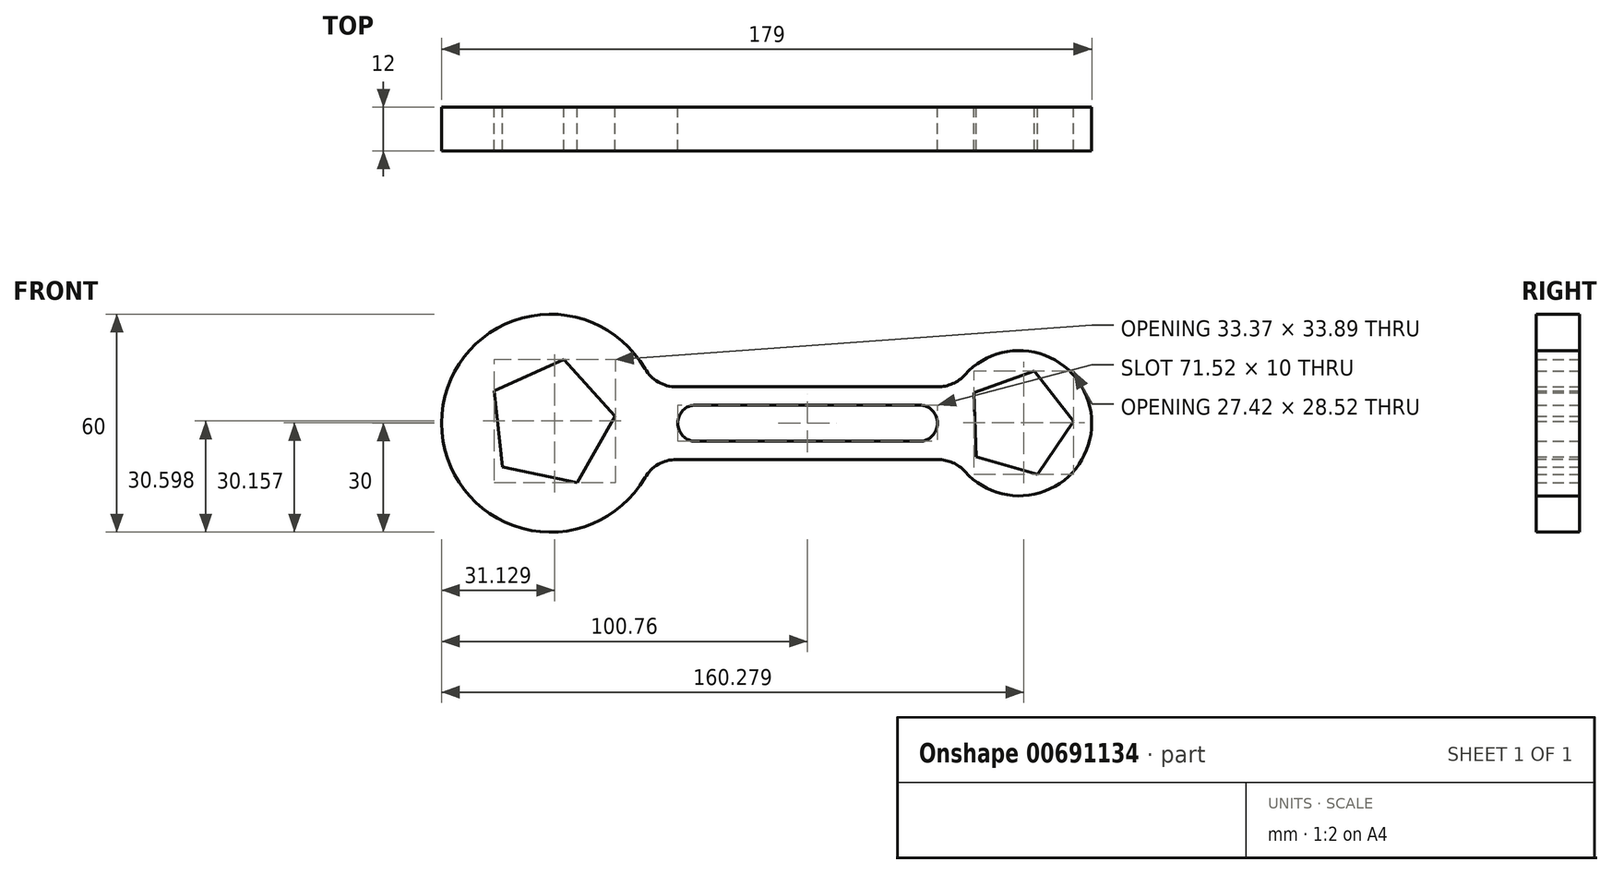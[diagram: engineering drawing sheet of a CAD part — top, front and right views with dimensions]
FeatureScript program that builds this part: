
annotation { "Feature Type Name" : "Feature", "Feature Type Description" : "" }
export const myFeature = defineFeature(function(context is Context, id is Id, definition is map)
    precondition{}
    {
        {
            var Q0;
            Q0=qCreatedBy(makeId("Front.planeOp"),FACE);
            var sketch = newSketch(context, id + "F0", { "sketchPlane" : qUnion([Q0])});
            skLineSegment(sketch, "E0.bottom", {"start": v(-42.92, 10) * mm, "end": v(40.48, 10) * mm});
            skLineSegment(sketch, "E0.top", {"start": v(-42.92, -10) * mm, "end": v(40.48, -10) * mm});
            skLineSegment(sketch, "E0.left", {"start": v(-42.92, 10) * mm, "end": v(-42.92, -10) * mm});
            skLineSegment(sketch, "E0.right", {"start": v(40.48, 10) * mm, "end": v(40.48, -10) * mm});
            skLineSegment(sketch, "E1.bottom", {"start": v(-31.2, 5) * mm, "end": v(30.32, 5) * mm});
            skLineSegment(sketch, "E1.top", {"start": v(-31.2, -5) * mm, "end": v(30.32, -5) * mm});
            skLineSegment(sketch, "E1.left", {"start": v(-31.2, 5) * mm, "end": v(-31.2, -5) * mm});
            skLineSegment(sketch, "E1.right", {"start": v(30.32, 5) * mm, "end": v(30.32, -5) * mm});
            skCircle(sketch, "E2", {"center": v(-31.2, 0) * mm, "radius": 5 * mm});
            skCircle(sketch, "E3", {"center": v(30.32, 0) * mm, "radius": 5 * mm});
            skCircle(sketch, "E4", {"center": v(-71.2, 0) * mm, "radius": 30 * mm});
            skCircle(sketch, "E5", {"center": v(57.8, 0) * mm, "radius": 20 * mm});
            skCircle(sketch, "E6.cCircle", {"center": v(-71.2, 0) * mm, "radius": 17.92 * mm, "construction": true});
            skLineSegment(sketch, "E6.0", {"start": v(-67.54, 17.54) * mm, "end": v(-53.39, 1.94) * mm});
            skLineSegment(sketch, "E6.1", {"start": v(-53.39, 1.94) * mm, "end": v(-63.86, -16.35) * mm});
            skLineSegment(sketch, "E6.2", {"start": v(-63.86, -16.35) * mm, "end": v(-84.48, -12.04) * mm});
            skLineSegment(sketch, "E6.3", {"start": v(-84.48, -12.04) * mm, "end": v(-86.75, 8.9) * mm});
            skLineSegment(sketch, "E6.4", {"start": v(-86.75, 8.9) * mm, "end": v(-67.54, 17.54) * mm});
            skCircle(sketch, "E7.cCircle", {"center": v(57.8, 0) * mm, "radius": 15 * mm, "construction": true});
            skLineSegment(sketch, "E7.0", {"start": v(61.95, 14.42) * mm, "end": v(72.8, 0.5) * mm});
            skLineSegment(sketch, "E7.1", {"start": v(72.8, 0.5) * mm, "end": v(62.91, -14.1) * mm});
            skLineSegment(sketch, "E7.2", {"start": v(62.91, -14.1) * mm, "end": v(45.97, -9.23) * mm});
            skLineSegment(sketch, "E7.3", {"start": v(45.97, -9.23) * mm, "end": v(45.37, 8.4) * mm});
            skLineSegment(sketch, "E7.4", {"start": v(45.37, 8.4) * mm, "end": v(61.95, 14.42) * mm});
            skSolve(sketch);
        }
        {
            var Q0;
            {var subQ1=sQuery(id+"F0.wireOp",EDGE,"E0.left");Q0=makeQuery(id+"F0.imprint","IMPRINT",FACE,{"disambiguationData":[TD([[makeQuery(id+"F0.imprint","IMPRINT",EDGE,{"derivedFrom":subQ1}),-1.0]])]});}
            var Q1;
            {var subQ3=sQuery(id+"F0.wireOp",EDGE,"E0.bottom");Q1=makeQuery(id+"F0.imprint","IMPRINT",FACE,{"disambiguationData":[TD([[makeQuery(id+"F0.imprint","IMPRINT",EDGE,{"derivedFrom":subQ3}),-1.0]])]});}
            var Q2;
            {var subQ0=sQuery(id+"F0.wireOp",EDGE,"E0.left");Q2=makeQuery(id+"F0.imprint","IMPRINT",FACE,{"disambiguationData":[TD([[makeQuery(id+"F0.imprint","IMPRINT",EDGE,{"derivedFrom":subQ0}),1.0]])]});}
            var Q3;
            {var subQ0=sQuery(id+"F0.wireOp",EDGE,"E0.right");Q3=makeQuery(id+"F0.imprint","IMPRINT",FACE,{"disambiguationData":[TD([[makeQuery(id+"F0.imprint","IMPRINT",EDGE,{"derivedFrom":subQ0}),-1.0]])]});}
            var Q4;
            {var subQ1=sQuery(id+"F0.wireOp",EDGE,"E0.right");Q4=makeQuery(id+"F0.imprint","IMPRINT",FACE,{"disambiguationData":[TD([[makeQuery(id+"F0.imprint","IMPRINT",EDGE,{"derivedFrom":subQ1}),1.0]])]});}
            extrude(context, id + "F1", {"entities" : qUnion([Q0, Q1, Q2, Q3, Q4]), "depth" : 12 * mm, "offsetDistance" : 25 * mm});
        }
        {
            var Q0;
            Q0=makeQuery(id+"F1.opExtrude","SWEPT_EDGE",EDGE,{"disambiguationData":[OSD([sQuery(id+"F0.wireOp",EDGE,"E0.top"),sQuery(id+"F0.wireOp",EDGE,"E0.left"),sQuery(id+"F0.wireOp",EDGE,"E4")])]});
            var Q1;
            Q1=makeQuery(id+"F1.opExtrude","SWEPT_EDGE",EDGE,{"disambiguationData":[OSD([sQuery(id+"F0.wireOp",EDGE,"E0.top"),sQuery(id+"F0.wireOp",EDGE,"E0.right"),sQuery(id+"F0.wireOp",EDGE,"E5")])]});
            var Q2;
            Q2=makeQuery(id+"F1.opExtrude","SWEPT_EDGE",EDGE,{"disambiguationData":[OSD([sQuery(id+"F0.wireOp",EDGE,"E0.bottom"),sQuery(id+"F0.wireOp",EDGE,"E0.right"),sQuery(id+"F0.wireOp",EDGE,"E5")])]});
            var Q3;
            Q3=makeQuery(id+"F1.opExtrude","SWEPT_EDGE",EDGE,{"disambiguationData":[OSD([sQuery(id+"F0.wireOp",EDGE,"E0.bottom"),sQuery(id+"F0.wireOp",EDGE,"E0.left"),sQuery(id+"F0.wireOp",EDGE,"E4")])]});
            fillet(context, id + "F2", {"entities" : qUnion([Q0, Q1, Q2, Q3]), "radius" : 10 * mm, "tangentPropagation" : true, "allowEdgeOverflow" : false});
        }
    });
